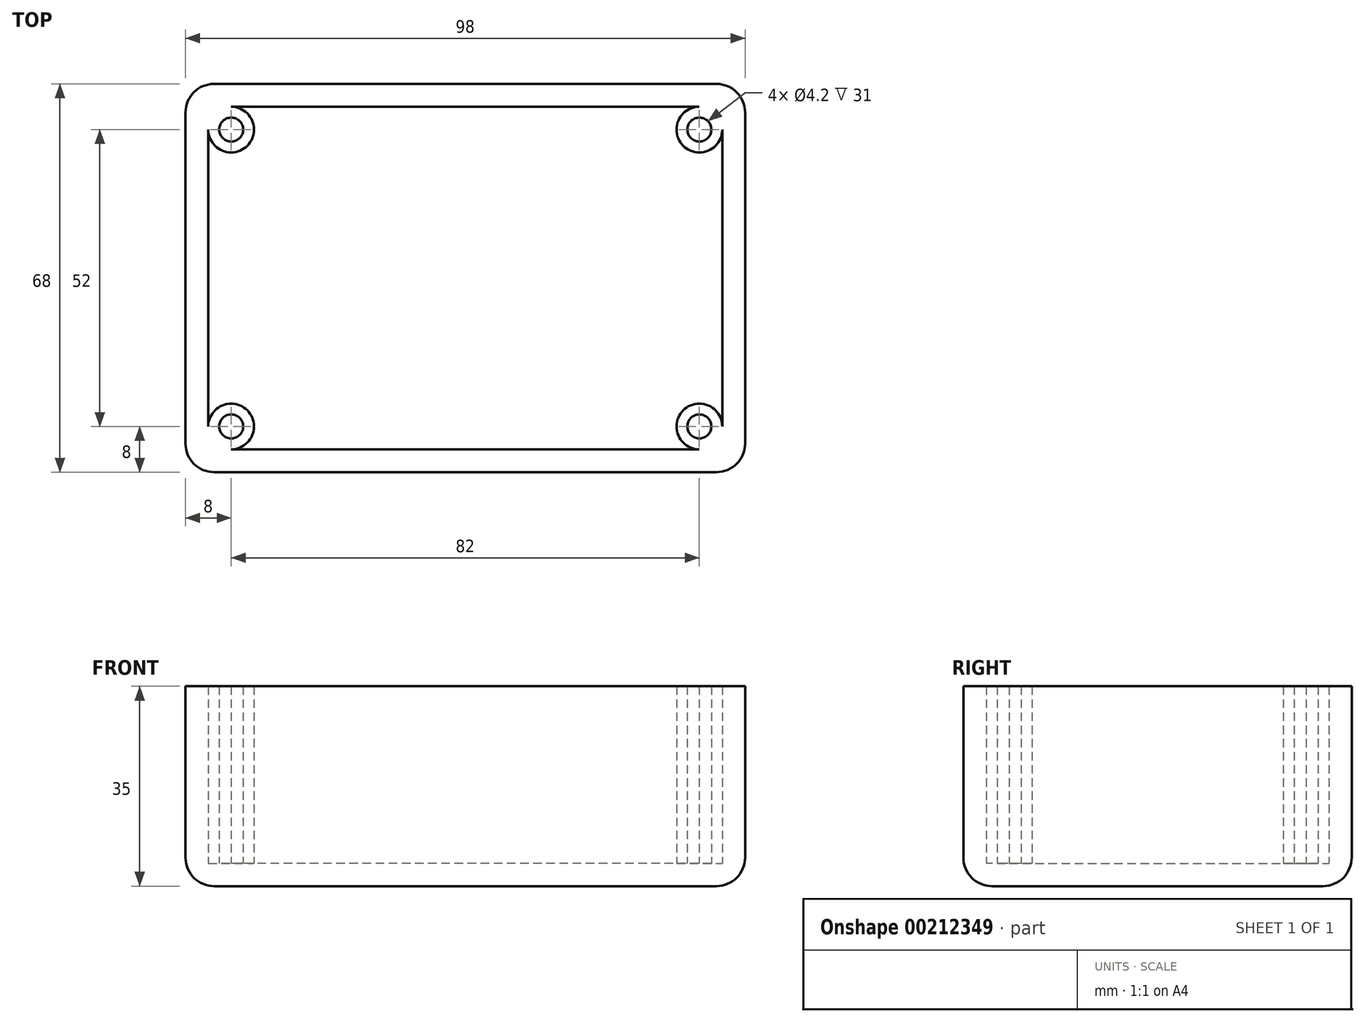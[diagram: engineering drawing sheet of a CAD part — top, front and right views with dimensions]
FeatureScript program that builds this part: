
annotation { "Feature Type Name" : "Feature", "Feature Type Description" : "" }
export const myFeature = defineFeature(function(context is Context, id is Id, definition is map)
    precondition{}
    {
        {
            var Q0;
            Q0=qCreatedBy(makeId("Top.planeOp"),FACE);
            var sketch = newSketch(context, id + "F0", { "sketchPlane" : qUnion([Q0])});
            skLineSegment(sketch, "E0.bottom", {"start": v(41, -30) * mm, "end": v(-41, -30) * mm});
            skLineSegment(sketch, "E0.top", {"start": v(41, 30) * mm, "end": v(-41, 30) * mm});
            skLineSegment(sketch, "E0.left", {"start": v(45, -26) * mm, "end": v(45, 26) * mm});
            skLineSegment(sketch, "E0.right", {"start": v(-45, -26) * mm, "end": v(-45, 26) * mm});
            skPoint(sketch, "E0.middle", {"position": v(0, 0) * mm});
            skLineSegment(sketch, "E1.bottom", {"start": v(49, -34) * mm, "end": v(-49, -34) * mm});
            skLineSegment(sketch, "E1.top", {"start": v(49, 34) * mm, "end": v(-49, 34) * mm});
            skLineSegment(sketch, "E1.left", {"start": v(49, -34) * mm, "end": v(49, 34) * mm});
            skLineSegment(sketch, "E1.right", {"start": v(-49, -34) * mm, "end": v(-49, 34) * mm});
            skCircle(sketch, "E2", {"center": v(-41, 26) * mm, "radius": 2.1 * mm});
            skArc(sketch, "E3", {"start": v(-45, 26) * mm, "mid": v(-38.17, 23.17) * mm, "end": v(-41, 30) * mm});
            skPoint(sketch, "E4.orphan", {"position": v(-45, 30) * mm});
            skCircle(sketch, "E5", {"center": v(41, 26) * mm, "radius": 2.1 * mm});
            skArc(sketch, "E6", {"start": v(41, 30) * mm, "mid": v(38.17, 23.17) * mm, "end": v(45, 26) * mm});
            skPoint(sketch, "E7.orphan", {"position": v(45, 30) * mm});
            skCircle(sketch, "E8", {"center": v(-41, -26) * mm, "radius": 2.1 * mm});
            skCircle(sketch, "E9", {"center": v(41, -26) * mm, "radius": 2.1 * mm});
            skArc(sketch, "E10", {"start": v(-41, -30) * mm, "mid": v(-38.17, -23.17) * mm, "end": v(-45, -26) * mm});
            skArc(sketch, "E11", {"start": v(45, -26) * mm, "mid": v(38.17, -23.17) * mm, "end": v(41, -30) * mm});
            skPoint(sketch, "E12.start.orphan", {"position": v(45, -30) * mm});
            skPoint(sketch, "E13.orphan", {"position": v(-45, -30) * mm});
            skSolve(sketch);
        }
        {
            var Q0;
            Q0 = qSketchRegion(id + "F0", true);
            extrude(context, id + "F1", {"entities" : qUnion([Q0]), "depth" : 35 * mm});
        }
        {
            var Q0;
            Q0=qCreatedBy(makeId("Top.planeOp"),FACE);
            var sketch = newSketch(context, id + "F2", { "sketchPlane" : qUnion([Q0])});
            skLineSegment(sketch, "E14.bottom", {"start": v(45, -30) * mm, "end": v(-45, -30) * mm});
            skLineSegment(sketch, "E14.top", {"start": v(45, 30) * mm, "end": v(-45, 30) * mm});
            skLineSegment(sketch, "E14.left", {"start": v(45, -30) * mm, "end": v(45, 30) * mm});
            skLineSegment(sketch, "E14.right", {"start": v(-45, -30) * mm, "end": v(-45, 30) * mm});
            skPoint(sketch, "E14.middle", {"position": v(0, 0) * mm});
            skSolve(sketch);
        }
        {
            var Q0;
            Q0 = qSketchRegion(id + "F2", true);
            var Q1;
            Q1 = qSketchRegion(id + "F0", true);
            extrude(context, id + "F3", {"entities" : qUnion([Q0, Q1]), "operationType" : NewBodyOperationType.ADD, "depth" : 4 * mm});
        }
        {
            var Q0;
            Q0=makeQuery(id+"F1.opExtrude","SWEPT_EDGE",EDGE,{"disambiguationData":[OSD([sQuery(id+"F0.wireOp",EDGE,"E1.bottom"),sQuery(id+"F0.wireOp",EDGE,"E1.left")])]});
            var Q1;
            Q1=makeQuery(id+"F1.opExtrude","SWEPT_EDGE",EDGE,{"disambiguationData":[OSD([sQuery(id+"F0.wireOp",EDGE,"E1.bottom"),sQuery(id+"F0.wireOp",EDGE,"E1.right")])]});
            var Q2;
            Q2=makeQuery(id+"F1.opExtrude","SWEPT_EDGE",EDGE,{"disambiguationData":[OSD([sQuery(id+"F0.wireOp",EDGE,"E1.top"),sQuery(id+"F0.wireOp",EDGE,"E1.right")])]});
            fillet(context, id + "F4", {"entities" : qUnion([Q0, Q1, Q2]), "radius" : 5 * mm, "tangentPropagation" : true, "allowEdgeOverflow" : false});
        }
        {
            var Q0;
            Q0=makeQuery(id+"F1.opExtrude","SWEPT_EDGE",EDGE,{"disambiguationData":[OSD([sQuery(id+"F0.wireOp",EDGE,"E1.top"),sQuery(id+"F0.wireOp",EDGE,"E1.left")])]});
            var Q1;
            Q1=makeQuery(id+"F1.opExtrude","CAP_EDGE",EDGE,{"disambiguationData":[OSD([sQuery(id+"F0.wireOp",EDGE,"E1.top")])],"isStart":true});
            fillet(context, id + "F5", {"entities" : qUnion([Q0, Q1]), "radius" : 5 * mm, "tangentPropagation" : true, "allowEdgeOverflow" : false});
        }
    });
